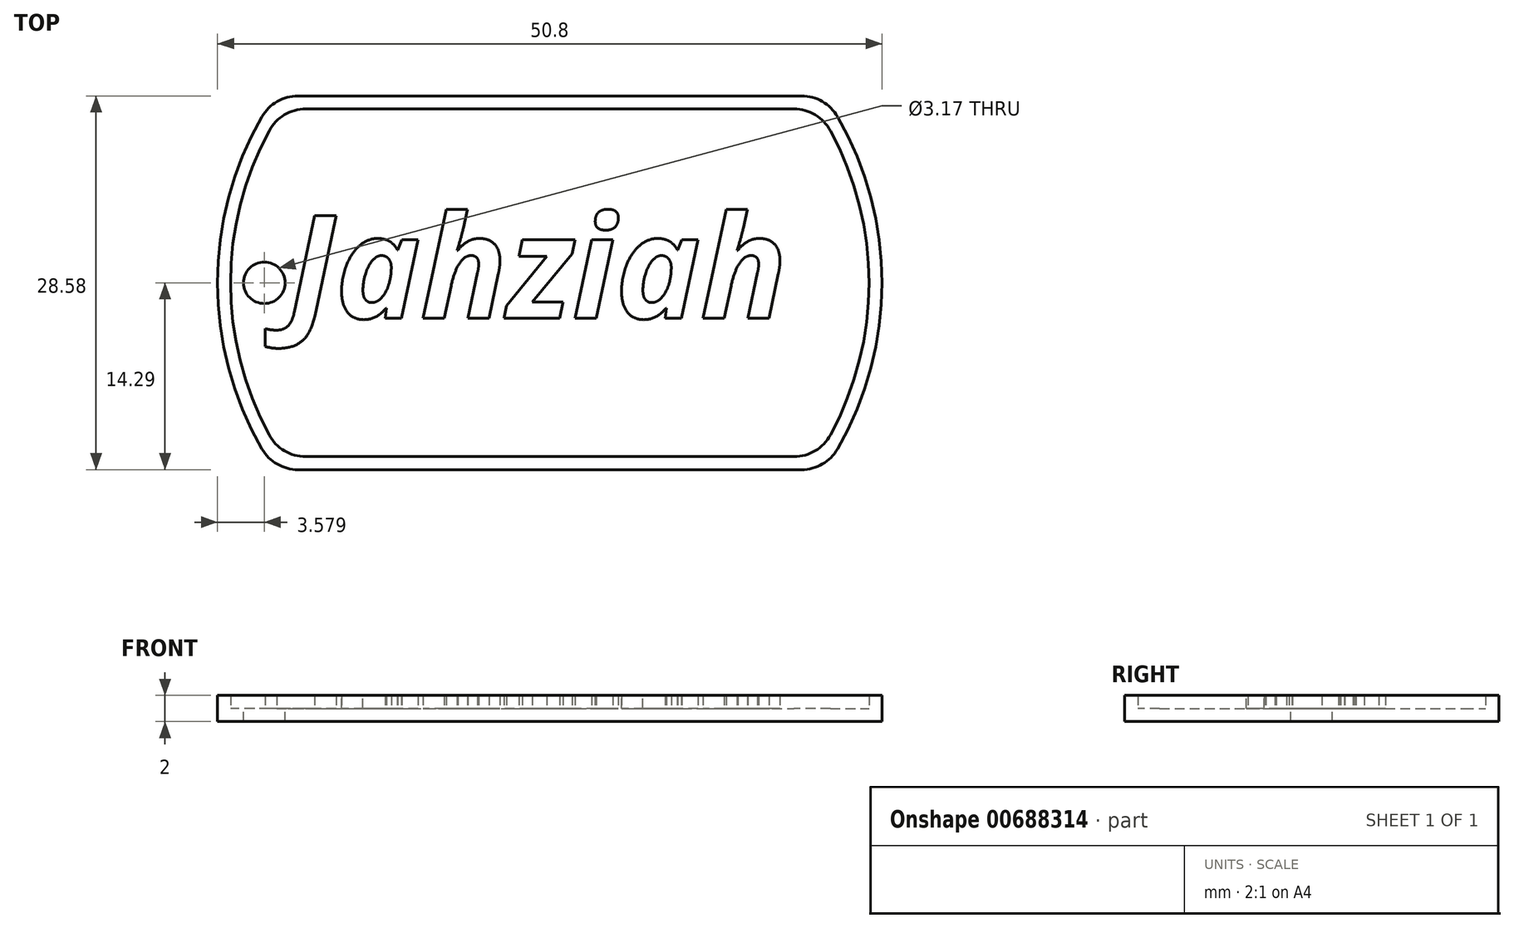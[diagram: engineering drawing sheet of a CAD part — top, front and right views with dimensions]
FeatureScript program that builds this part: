
annotation { "Feature Type Name" : "Feature", "Feature Type Description" : "" }
export const myFeature = defineFeature(function(context is Context, id is Id, definition is map)
    precondition{}
    {
        {
            var Q0;
            Q0=qCreatedBy(makeId("Top.planeOp"),FACE);
            var sketch = newSketch(context, id + "F0", { "sketchPlane" : qUnion([Q0])});
            skArc(sketch, "E0", {"start": v(-22, 12.7) * mm, "mid": v(-25.4, 0) * mm, "end": v(-22, -12.7) * mm});
            skLineSegment(sketch, "E1.top", {"start": v(-19.25, -14.29) * mm, "end": v(19.25, -14.29) * mm});
            skArc(sketch, "E2.trimOffspring", {"start": v(22, -12.7) * mm, "mid": v(25.4, 0) * mm, "end": v(22, 12.7) * mm});
            skLineSegment(sketch, "E3", {"start": v(-19.25, 14.29) * mm, "end": v(19.25, 14.29) * mm});
            skPoint(sketch, "E4.visualSharp", {"position": v(-21, 14.29) * mm});
            skArc(sketch, "E4.filletArc", {"start": v(-19.25, 14.29) * mm, "mid": v(-20.83, 13.86) * mm, "end": v(-22, 12.7) * mm});
            skPoint(sketch, "E5.visualSharp", {"position": v(21, 14.29) * mm});
            skArc(sketch, "E5.filletArc", {"start": v(22, 12.7) * mm, "mid": v(20.83, 13.86) * mm, "end": v(19.25, 14.29) * mm});
            skPoint(sketch, "E6.visualSharp", {"position": v(21, -14.29) * mm});
            skArc(sketch, "E6.filletArc", {"start": v(19.25, -14.29) * mm, "mid": v(20.83, -13.86) * mm, "end": v(22, -12.7) * mm});
            skPoint(sketch, "E7.visualSharp", {"position": v(-21, -14.29) * mm});
            skArc(sketch, "E7.filletArc", {"start": v(-22, -12.7) * mm, "mid": v(-20.83, -13.86) * mm, "end": v(-19.25, -14.29) * mm});
            skSolve(sketch);
        }
        {
            var Q0;
            Q0=makeQuery(id+"F0.imprint","IMPRINT",FACE,{"disambiguationData":[TD([[makeQuery(id+"F0.imprint","IMPRINT",EDGE,{"derivedFrom":sQuery(id+"F0.wireOp",EDGE,"E0")}),1.0]])]});
            extrude(context, id + "F1", {"entities" : qUnion([Q0]), "depth" : 1 * mm, "offsetDistance" : 25.4 * mm});
        }
        {
            var Q0;
            Q0=makeQuery(id+"F1.opExtrude","CAP_FACE",FACE,{"disambiguationData":[OSD([sQuery(id+"F0.wireOp",EDGE,"E0"),sQuery(id+"F0.wireOp",EDGE,"E1.top"),sQuery(id+"F0.wireOp",EDGE,"E2.trimOffspring"),sQuery(id+"F0.wireOp",EDGE,"E3"),sQuery(id+"F0.wireOp",EDGE,"E4.filletArc"),sQuery(id+"F0.wireOp",EDGE,"E5.filletArc"),sQuery(id+"F0.wireOp",EDGE,"E6.filletArc"),sQuery(id+"F0.wireOp",EDGE,"E7.filletArc")])],"isStart":false});
            var sketch = newSketch(context, id + "F2", { "sketchPlane" : qUnion([Q0])});
            skLineSegment(sketch, "E8.0", {"start": v(-18.66, 13.29) * mm, "end": v(18.66, 13.29) * mm});
            skArc(sketch, "E8.1", {"start": v(-21.45, 11.63) * mm, "mid": v(-24.4, 0) * mm, "end": v(-21.45, -11.63) * mm});
            skLineSegment(sketch, "E8.2", {"start": v(-18.66, -13.29) * mm, "end": v(18.66, -13.29) * mm});
            skArc(sketch, "E8.3", {"start": v(21.45, -11.63) * mm, "mid": v(24.4, 0) * mm, "end": v(21.45, 11.63) * mm});
            skPoint(sketch, "E9.visualSharp", {"position": v(-20.46, 13.29) * mm});
            skArc(sketch, "E9.filletArc", {"start": v(-18.66, 13.29) * mm, "mid": v(-20.29, 12.84) * mm, "end": v(-21.45, 11.63) * mm});
            skPoint(sketch, "E10.visualSharp", {"position": v(20.46, 13.29) * mm});
            skArc(sketch, "E10.filletArc", {"start": v(21.45, 11.63) * mm, "mid": v(20.29, 12.84) * mm, "end": v(18.66, 13.29) * mm});
            skPoint(sketch, "E11.visualSharp", {"position": v(20.46, -13.29) * mm});
            skArc(sketch, "E11.filletArc", {"start": v(18.66, -13.29) * mm, "mid": v(20.29, -12.84) * mm, "end": v(21.45, -11.63) * mm});
            skPoint(sketch, "E12.visualSharp", {"position": v(-20.46, -13.29) * mm});
            skArc(sketch, "E12.filletArc", {"start": v(-21.45, -11.63) * mm, "mid": v(-20.29, -12.84) * mm, "end": v(-18.66, -13.29) * mm});
            skLineSegment(sketch, "E13.0", {"start": v(-19.25, 14.29) * mm, "end": v(19.25, 14.29) * mm});
            skArc(sketch, "E13.1", {"start": v(-22, 12.7) * mm, "mid": v(-25.4, 0) * mm, "end": v(-22, -12.7) * mm});
            skLineSegment(sketch, "E13.2", {"start": v(-19.25, -14.29) * mm, "end": v(19.25, -14.29) * mm});
            skArc(sketch, "E13.3", {"start": v(22, -12.7) * mm, "mid": v(25.4, 0) * mm, "end": v(22, 12.7) * mm});
            skPoint(sketch, "E14.visualSharp", {"position": v(-21, -14.29) * mm});
            skArc(sketch, "E14.filletArc", {"start": v(-22, -12.7) * mm, "mid": v(-20.83, -13.86) * mm, "end": v(-19.25, -14.29) * mm});
            skPoint(sketch, "E15.visualSharp", {"position": v(21, -14.29) * mm});
            skArc(sketch, "E15.filletArc", {"start": v(19.25, -14.29) * mm, "mid": v(20.83, -13.86) * mm, "end": v(22, -12.7) * mm});
            skPoint(sketch, "E16.visualSharp", {"position": v(21, 14.29) * mm});
            skArc(sketch, "E16.filletArc", {"start": v(22, 12.7) * mm, "mid": v(20.83, 13.86) * mm, "end": v(19.25, 14.29) * mm});
            skPoint(sketch, "E17.visualSharp", {"position": v(-21, 14.29) * mm});
            skArc(sketch, "E17.filletArc", {"start": v(-19.25, 14.29) * mm, "mid": v(-20.83, 13.86) * mm, "end": v(-22, 12.7) * mm});
            skSolve(sketch);
        }
        {
            var Q0;
            Q0=makeQuery(id+"F2.imprint","IMPRINT",FACE,{"disambiguationData":[TD([[makeQuery(id+"F2.imprint","IMPRINT",EDGE,{"derivedFrom":sQuery(id+"F2.wireOp",EDGE,"E8.0")}),1.0]])]});
            extrude(context, id + "F3", {"entities" : qUnion([Q0]), "operationType" : NewBodyOperationType.ADD, "depth" : 1 * mm, "offsetDistance" : 25.4 * mm});
        }
        {
            var Q0;
            Q0=makeQuery(id+"F1.opExtrude","CAP_FACE",FACE,{"disambiguationData":[OSD([sQuery(id+"F0.wireOp",EDGE,"E0"),sQuery(id+"F0.wireOp",EDGE,"E1.top"),sQuery(id+"F0.wireOp",EDGE,"E2.trimOffspring"),sQuery(id+"F0.wireOp",EDGE,"E3"),sQuery(id+"F0.wireOp",EDGE,"E4.filletArc"),sQuery(id+"F0.wireOp",EDGE,"E5.filletArc"),sQuery(id+"F0.wireOp",EDGE,"E6.filletArc"),sQuery(id+"F0.wireOp",EDGE,"E7.filletArc")])],"isStart":false});
            var sketch = newSketch(context, id + "F4", { "sketchPlane" : qUnion([Q0])});
            skCircle(sketch, "E18", {"center": v(-21.82, 0) * mm, "radius": 1.59 * mm});
            skSolve(sketch);
        }
        {
            var Q0;
            Q0=makeQuery(id+"F4.imprint","IMPRINT",FACE,{"disambiguationData":[TD([[makeQuery(id+"F4.imprint","IMPRINT",EDGE,{"derivedFrom":sQuery(id+"F4.wireOp",EDGE,"E18")}),1.0]])]});
            extrude(context, id + "F5", {"entities" : qUnion([Q0]), "operationType" : NewBodyOperationType.REMOVE, "oppositeDirection" : true, "depth" : 1 * mm, "offsetDistance" : 25.4 * mm});
        }
        {
            var Q0;
            Q0=makeQuery(id+"F2.imprint","IMPRINT",FACE,{"disambiguationData":[TD([[makeQuery(id+"F2.imprint","IMPRINT",EDGE,{"derivedFrom":sQuery(id+"F2.wireOp",EDGE,"E8.0")}),-1.0]])]});
            var sketch = newSketch(context, id + "F6", { "sketchPlane" : qUnion([Q0])});
            skText(sketch, "E19", { "text": "Jahziah", "fontName": "OpenSans-BoldItalic.ttf"});
            const initialGuessF6  = {"E19": [-0.02003, -0.00271, 1, 0, 0.0079]};
            skSetInitialGuess(sketch, initialGuessF6);
            skSolve(sketch);
        }
        {
            var Q0;
            Q0 = qSketchRegion(id + "F6", true);
            extrude(context, id + "F7", {"entities" : qUnion([Q0]), "operationType" : NewBodyOperationType.ADD, "depth" : 1 * mm, "offsetDistance" : 25.4 * mm});
        }
    });
